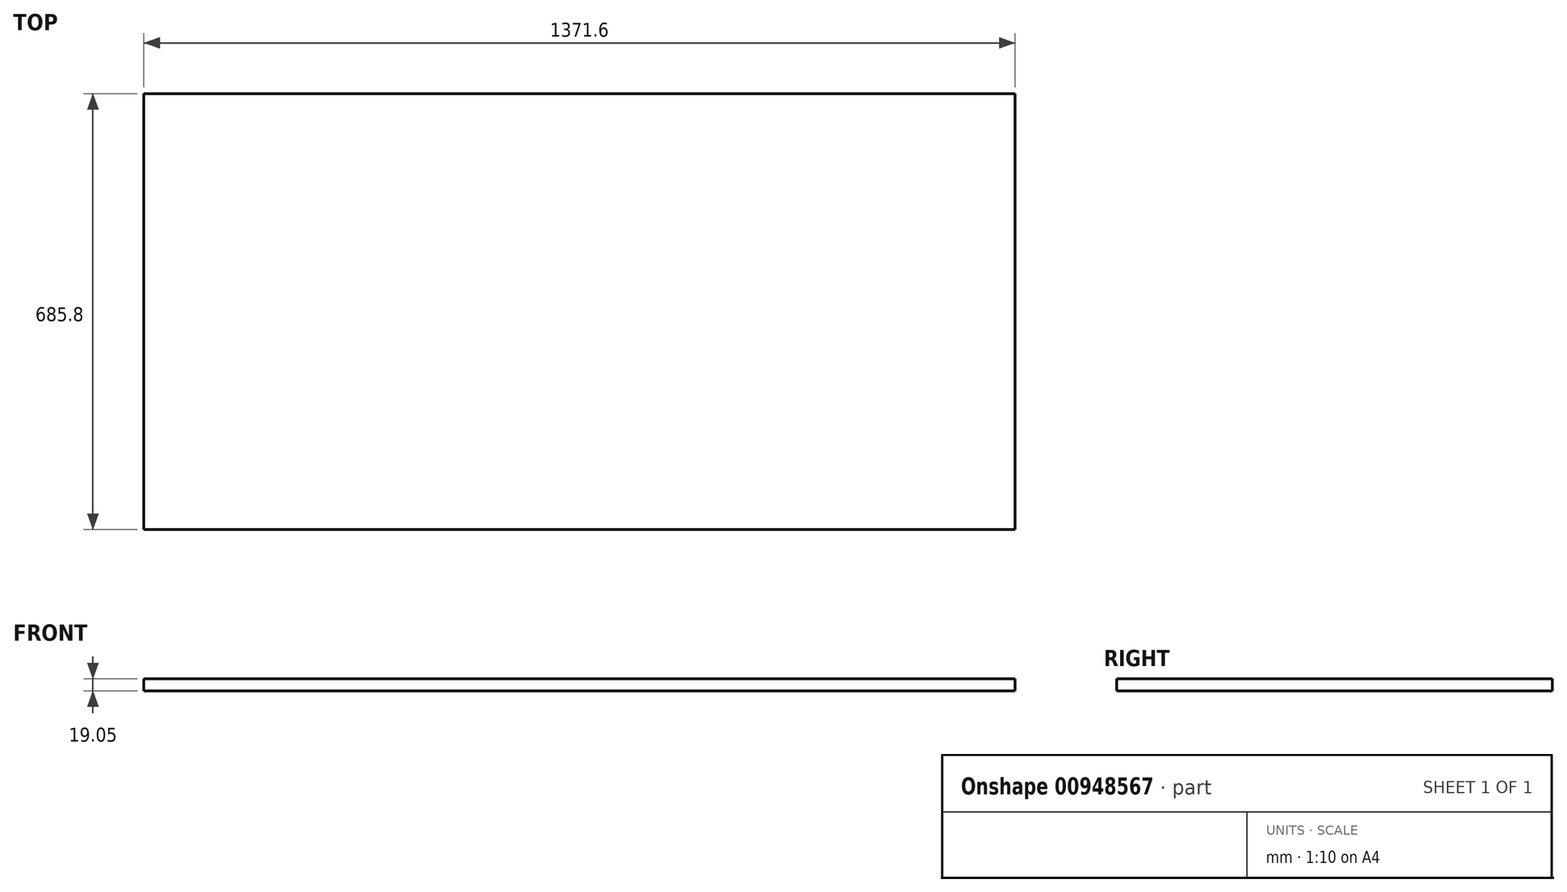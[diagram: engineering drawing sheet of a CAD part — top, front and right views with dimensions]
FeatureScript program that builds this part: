
annotation { "Feature Type Name" : "Feature", "Feature Type Description" : "" }
export const myFeature = defineFeature(function(context is Context, id is Id, definition is map)
    precondition{}
    {
        {
            var Q0;
            Q0=qCreatedBy(makeId("Top.planeOp"),FACE);
            var sketch = newSketch(context, id + "F0", { "sketchPlane" : qUnion([Q0])});
            skLineSegment(sketch, "E0.bottom", {"start": v(685.8, 342.9) * mm, "end": v(-685.8, 342.9) * mm});
            skLineSegment(sketch, "E0.top", {"start": v(685.8, -342.9) * mm, "end": v(-685.8, -342.9) * mm});
            skLineSegment(sketch, "E0.left", {"start": v(685.8, 342.9) * mm, "end": v(685.8, -342.9) * mm});
            skLineSegment(sketch, "E0.right", {"start": v(-685.8, 342.9) * mm, "end": v(-685.8, -342.9) * mm});
            skPoint(sketch, "E0.middle", {"position": v(0, 0) * mm});
            skSolve(sketch);
        }
        {
            var Q0;
            Q0=makeQuery(id+"F0.imprint","IMPRINT",FACE,{"disambiguationData":[TD([[makeQuery(id+"F0.imprint","IMPRINT",EDGE,{"derivedFrom":sQuery(id+"F0.wireOp",EDGE,"E0.bottom")}),1.0]])]});
            extrude(context, id + "F1", {"entities" : qUnion([Q0]), "depth" : 19.05 * mm, "offsetDistance" : 25.4 * mm});
        }
    });
